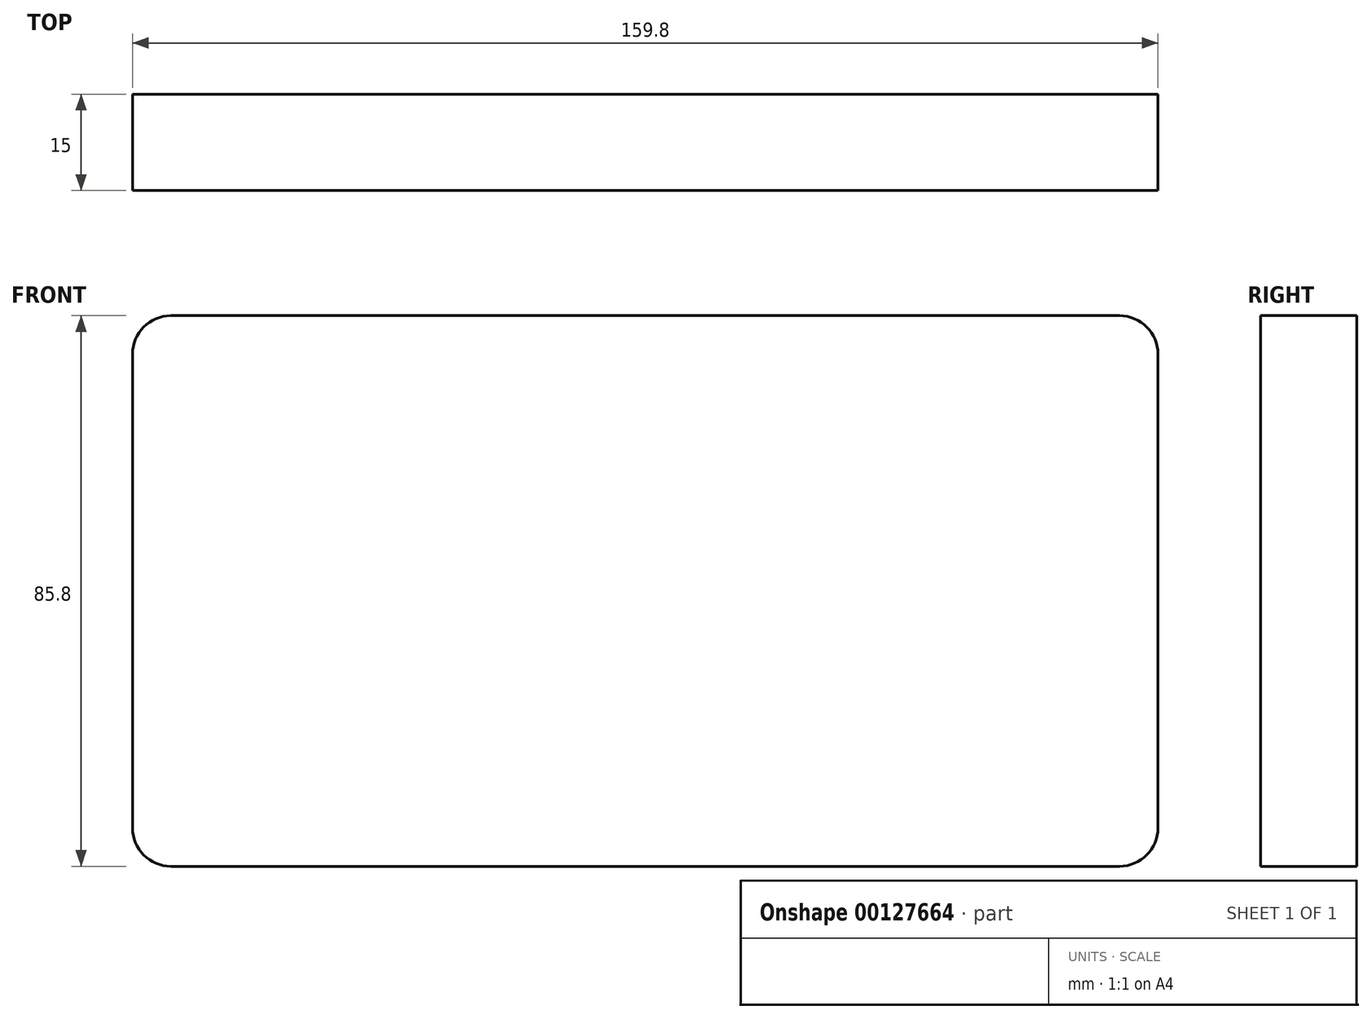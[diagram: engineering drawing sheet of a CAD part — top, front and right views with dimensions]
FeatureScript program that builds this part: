
annotation { "Feature Type Name" : "Feature", "Feature Type Description" : "" }
export const myFeature = defineFeature(function(context is Context, id is Id, definition is map)
    precondition{}
    {
        {
            var Q0;
            Q0=qCreatedBy(makeId("Front.planeOp"),FACE);
            var sketch = newSketch(context, id + "F0", { "sketchPlane" : qUnion([Q0])});
            skLineSegment(sketch, "E0.bottom", {"start": v(73.9, 42.9) * mm, "end": v(-73.9, 42.9) * mm});
            skLineSegment(sketch, "E0.top", {"start": v(73.9, -42.9) * mm, "end": v(-73.9, -42.9) * mm});
            skLineSegment(sketch, "E0.left", {"start": v(79.9, 36.9) * mm, "end": v(79.9, -36.9) * mm});
            skLineSegment(sketch, "E0.right", {"start": v(-79.9, 36.9) * mm, "end": v(-79.9, -36.9) * mm});
            skPoint(sketch, "E0.middle", {"position": v(0, 0) * mm});
            skPoint(sketch, "E1.visualSharp", {"position": v(-79.9, 42.9) * mm});
            skArc(sketch, "E1.filletArc", {"start": v(-73.9, 42.9) * mm, "mid": v(-78.14, 41.14) * mm, "end": v(-79.9, 36.9) * mm});
            skPoint(sketch, "E2.visualSharp", {"position": v(-79.9, -42.9) * mm});
            skArc(sketch, "E2.filletArc", {"start": v(-79.9, -36.9) * mm, "mid": v(-78.14, -41.14) * mm, "end": v(-73.9, -42.9) * mm});
            skPoint(sketch, "E3.visualSharp", {"position": v(79.9, -42.9) * mm});
            skArc(sketch, "E3.filletArc", {"start": v(73.9, -42.9) * mm, "mid": v(78.14, -41.14) * mm, "end": v(79.9, -36.9) * mm});
            skPoint(sketch, "E4.visualSharp", {"position": v(79.9, 42.9) * mm});
            skArc(sketch, "E4.filletArc", {"start": v(79.9, 36.9) * mm, "mid": v(78.14, 41.14) * mm, "end": v(73.9, 42.9) * mm});
            skSolve(sketch);
        }
        {
            var Q0;
            Q0 = qSketchRegion(id + "F0", true);
            extrude(context, id + "F1", {"entities" : qUnion([Q0]), "depth" : 15 * mm});
        }
    });
